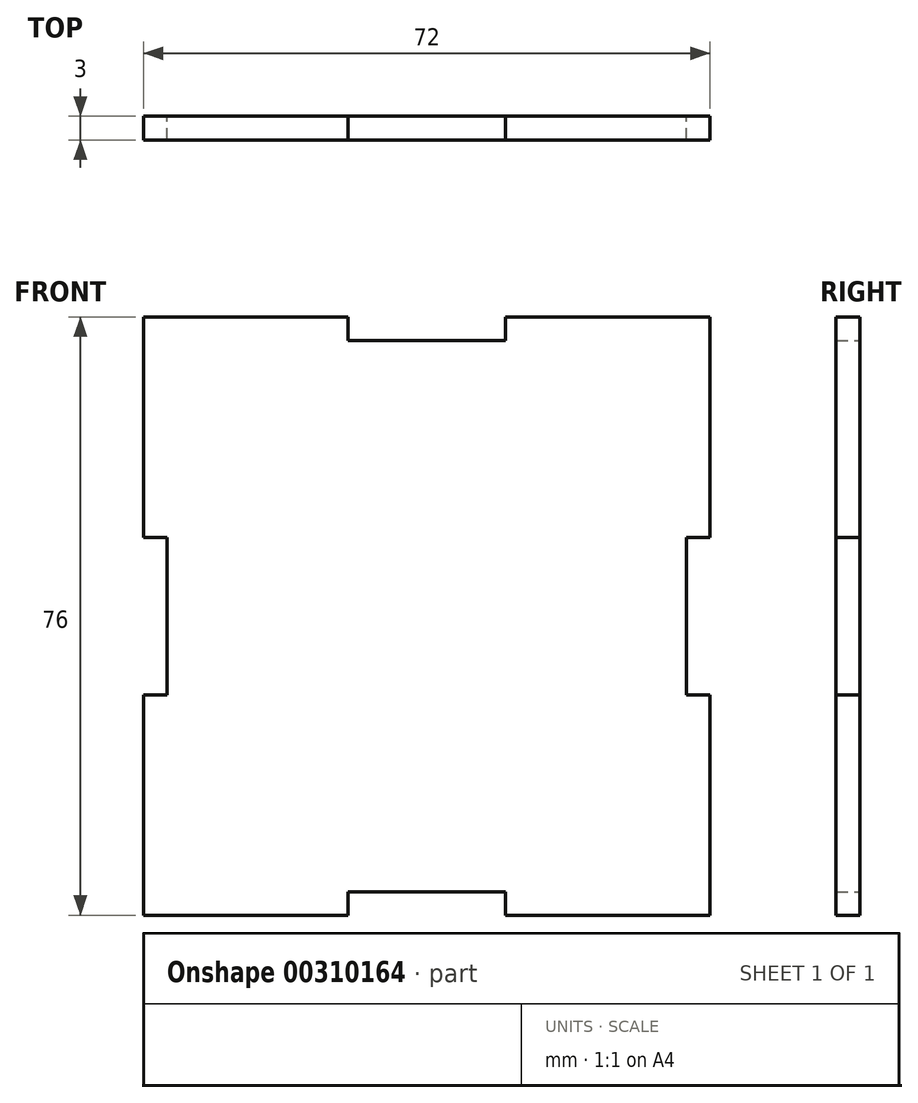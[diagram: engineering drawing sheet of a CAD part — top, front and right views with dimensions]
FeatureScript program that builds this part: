
annotation { "Feature Type Name" : "Feature", "Feature Type Description" : "" }
export const myFeature = defineFeature(function(context is Context, id is Id, definition is map)
    precondition{}
    {
        {
            var Q0;
            Q0=qCreatedBy(makeId("Front.planeOp"),FACE);
            var sketch = newSketch(context, id + "F0", { "sketchPlane" : qUnion([Q0])});
            skLineSegment(sketch, "E0.bottom", {"start": v(36, -38) * mm, "end": v(10, -38) * mm});
            skLineSegment(sketch, "E0.top", {"start": v(36, 38) * mm, "end": v(10, 38) * mm});
            skLineSegment(sketch, "E0.left", {"start": v(36, -38) * mm, "end": v(36, -10) * mm});
            skLineSegment(sketch, "E0.right", {"start": v(-36, -38) * mm, "end": v(-36, -10) * mm});
            skPoint(sketch, "E0.middle", {"position": v(0, 0) * mm});
            skLineSegment(sketch, "E1.top", {"start": v(-10, 35) * mm, "end": v(10, 35) * mm});
            skLineSegment(sketch, "E1.left", {"start": v(-10, 38) * mm, "end": v(-10, 35) * mm});
            skLineSegment(sketch, "E1.right", {"start": v(10, 38) * mm, "end": v(10, 35) * mm});
            skLineSegment(sketch, "E2.bottom", {"start": v(-36, 10) * mm, "end": v(-33, 10) * mm});
            skLineSegment(sketch, "E2.top", {"start": v(-36, -10) * mm, "end": v(-33, -10) * mm});
            skLineSegment(sketch, "E2.right", {"start": v(-33, 10) * mm, "end": v(-33, -10) * mm});
            skLineSegment(sketch, "E3.trimOffspring", {"start": v(-10, 38) * mm, "end": v(-36, 38) * mm});
            skLineSegment(sketch, "E4.trimOffspring", {"start": v(-36, 10) * mm, "end": v(-36, 38) * mm});
            skLineSegment(sketch, "E5.MirrorCS", {"start": v(10, -38) * mm, "end": v(10, -35) * mm});
            skLineSegment(sketch, "E6.MirrorCS", {"start": v(-10, -38) * mm, "end": v(-10, -35) * mm});
            skLineSegment(sketch, "E7.MirrorCS", {"start": v(-10, -35) * mm, "end": v(10, -35) * mm});
            skLineSegment(sketch, "E8.MirrorCS", {"start": v(36, 10) * mm, "end": v(33, 10) * mm});
            skLineSegment(sketch, "E9.MirrorCS", {"start": v(33, 10) * mm, "end": v(33, -10) * mm});
            skLineSegment(sketch, "E10.MirrorCS", {"start": v(36, -10) * mm, "end": v(33, -10) * mm});
            skLineSegment(sketch, "E11.trimOffspring", {"start": v(36, 10) * mm, "end": v(36, 38) * mm});
            skLineSegment(sketch, "E12.trimOffspring", {"start": v(-10, -38) * mm, "end": v(-36, -38) * mm});
            skSolve(sketch);
        }
        {
            var Q0;
            Q0 = qSketchRegion(id + "F0", true);
            extrude(context, id + "F1", {"entities" : qUnion([Q0]), "depth" : 3 * mm});
        }
    });
